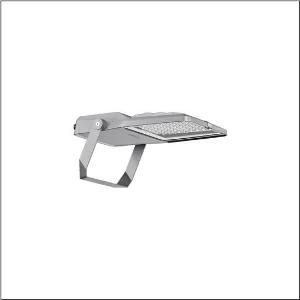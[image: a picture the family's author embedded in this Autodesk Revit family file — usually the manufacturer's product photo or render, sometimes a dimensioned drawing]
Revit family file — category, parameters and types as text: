
# Revit family: floodlight_fl_21_iq_mini___rs12_5xa7772b2b1a_75ed
name_source: partatom
category: Lighting Fixtures
units: mm (PartAtom-declared; Revit-internal decimal feet)

## family parameters
Cut with Voids When Loaded = No
Host = Face
Light Source = No
Part Type = Normal
Room Calculation Point = No
Round Connector Dimension = Use Diameter
Shared = No

## types (1)
- --- (1 x LED, 6300 lm, 45.5 W, 3000K)
    Apparent Load = 46 VA
    CIE Flux Codes = 79 92 99 100 100
    Color Rendering = 70
    Color Temperature = 3000K
    Default Elevation = 1800 mm
    Description = Floodlight FL 21 iQ mini, floodlight, primary light control with lens, of PMMA, primary optical cover: protective disc, of toughened safety glass, transparent, light distribution: RS12, light emission: direct distribution, installation type: surface-mounted, lamps: LED, High Power LED, rated values: 6.300lm | 45,5W | 138,5lm/W (begin service life); end service life: 6.300lm | 48W; at 50% lumin. flux: 3.150lm | 21,5W | 146,5lm/W, colour temperature: 3000K, colour rendering: CRI > 70, light colour: 730, light setting 1 begin service life: 100% | 6.300lm | 45,5W | 138,5lm/W | 3.000K, light setting 1 end service life: 48W, further light settings possible, control: Street-Remote, Auto-Match, Temp-Guard, Night-Set, Smart-Wire, Desk-Remote (wireless, voltage-free reading and setting of iQ features in the workshop via application-optimized NFC function/RFID function), optimised constant luminous flux control (CLO 2.0), pre-setting: linear dimming characteristic, with terminal, 6-pole, mains connection: 220..240V, AC, 50/60Hz, luminaire housing, of diecast aluminium, powder-coated, SITECO metallic grey (DB 702S), corrosivity category C5 mid according to DIN EN ISO 12944suitable for swimming poolschlorine-resistant, sealing non-destructively replaceable, mounting bracket, of steel, galvanised, powder-coated, SITECO metallic grey (DB 702S), protection rating (complete): IP66, insulation class (complete): insulation class II (safety insulation), certification: CE, ENEC, VDE, protection symbol: D, impact resistance: IK08, permissible operating ambient temperature: -40..+40°C, permissible operating ambient temperature for outdoor applications: -40..+50°C, standard: DIN EN 12944, LABS conformity tested according to VDMA 24364:2018-05, packaging unit: 1 piece

Light Distribution: RS12
    Height = 70 mm
    Lamp = 1 x LED
    Lamp Light Flux = 6300 lm
    Lamp Power = 45.5 W
    Lamp count = 1
    Length = 485 mm
    Luminous efficacy = 138 lm/W
    Manufacturer = Siteco
    ModVariant = No
    Model = 5XA7772B2B1A
    Mounting Place = Pole
    Mounting Type = Pole annexe
    Number of Poles = 1
    OnlyDefault = Yes
    Power Factor = 1
    Product Name = Floodlight FL 21 iQ mini | RS12
    Product group = floodlight | pylon annexe
    ProductGroupID = 6201
    Protection Class = Protection class II
    Protection Degree = IP 66
    RLX_Detail_Level = 1
    RLX_Emergency_Light_Flux = 0 lm
    RLX_Emergency_Type = 0
    RLX_Emergency_Type_DB = No
    RlxData = <blob elided: 91017 chars, md5=b9ae2f45>
    Socket = socket
    Standby Power = 0 W
    System Light Flux = 6300 lm
    System Power = 46 W
    Type Comments = factory setting: luminous flux: 100 % | dim-lin: 254 | 463 mA
    Type Image = l_1006845.jpg
    URL = http://relux.com
    VarID = @adj_168921
    Voltage = 0 V
    Weight = 0.00 kg
    Width = 337 mm

## geometry (parser evidence)
native form markers: Blend x4, Sweep x13
no freeform markers — native parametric forms only
